# Revit family: ASH_Contour21_S6487_BIM_GB
name_source: partatom
category: Plumbing Fixtures
revit_build: Autodesk Revit MEP 2014 (Build: 20130308_1515(x64)
units: mm (PartAtom-declared; Revit-internal decimal feet)

## types (2) — shared parameters
AccessibilityPerformance = Part-M
Accessories = www.idealspec.co.uk
AreaUnits = millimeters
Assembly Code = C1030200
AssetType = Fixed
Brand = Armitage Shanks
ConnectionType = Plumbing
Default Elevation = 680 mm  [stored 2.23097 ft]
Description = Contour 21 contemporary grab rail angled 45x 45cm long
DurationUnit = year
ExpectedLife = 30
Features = Contemporary grab rail angled 45x 45cm long
Finish = Chrome
IfcExportAs = IfcValveType
IfcExportType = FAUCET
InstallationInstructions = www.idealspec.co.uk/resources.html
LinearUnits = millimeters
ManufacturerURL = www.idealspec.co.uk
Material = Aluminium
ModelReference = Contour 21 contemporary grab rail angled 45x 45cm long
NBSDescription = Support rails
NBSReference = 45-35-70/360
NettWeight = 0.62 Kg
Shape = Sculptured
Size = 0 x 0 x 0 mm
Space = Internal
SpareParts = www.fastpart-spares.co.uk
URL = www.idealspec.co.uk
Uniclass2015Code = Pr_40_20_76_84
Uniclass2015Title = Support rails
Uniclass2015Version = Products v1.1
Version = 1
VolumeUnits = Litres
WarrantyDescription = Manufacturers Warranty
WarrantyDurationParts = 5
WarrantyDurationUnit = year
zero-valued in all types: CWFU, Cost, HWFU, NominalHeight, NominalLength, NominalWidth, WFU

## per-type parameters (varying)
| type | BIMObjectName | BarCode | Color | GrabRailMtl | Model | ModelNumber | Name | ProductInformation |
| S6487AA - Contour21 - Contemporary Grab Rail - 450 x 450mm Angled - Chrome | ASH_ArmitageShanks_SupportRails_Contour21_S6487AA | 5017830387374 | Chrome finish | ASH_ArmatigeShanks_Brassware_Chrome_Render | S6487AA | S6487AA | SupportRails_Contour21_S6487AA_ArmitageShanks | www.idealspec.co.uk/assets/datasheet/S6487AA |
| S6487MY - Contour21 - Contemporary Grab Rail - 450 x 450mm Angled - Stainless Steel | ASH_ArmitageShanks_SupportRails_Contour21_S6487MY | 5017830387404 | Stainless Steel finish | ASH_ArmatigeShanks_Brassware_Steel_Render | S6487MY | S6487MY | SupportRails_Contour21_S6487MY_ArmitageShanks | www.idealspec.co.uk/assets/datasheet/S6487MY |

note: [stored X ft] marks values corroborated as IEEE doubles in the binary element streams (Revit-internal decimal feet)

## geometry (parser evidence)
native form markers: Sweep x5
no freeform markers — native parametric forms only
